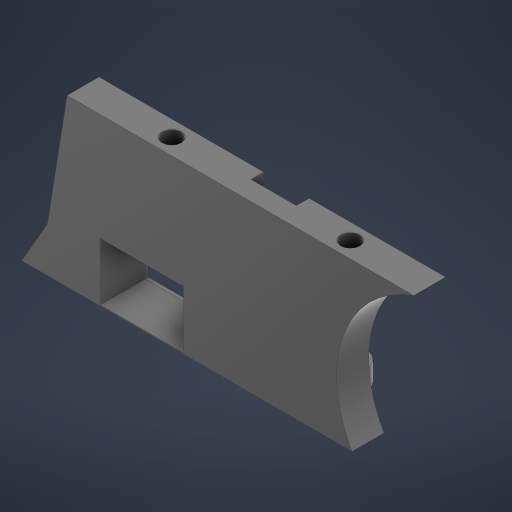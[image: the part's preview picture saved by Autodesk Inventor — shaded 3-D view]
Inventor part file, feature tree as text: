
AUTODESK INVENTOR PART (.ipt)
format: ipt  version: 2024 (Build 280153000, 153)  size: 302,080 bytes
history: native  units: in
note: dims shown in document units (in); Inventor stores cm internally (conversion verified against a paired STEP export)
features: extrude x7, sketch x7, chamfer x2, fillet x1
ambient origin geometry x8: Origin, YZ Plane, XZ Plane, XY Plane, X Axis, Y Axis, Z Axis, Center Point
bodies: Solid1 (feature_tree)
feature tree (17):
  extrude  "Extrusion1"  Depth=0.315in
  extrude  "Extrusion4"  Depth=0.1969in TaperAngle=0.0deg
  chamfer  "Chamfer2"  Distance=0.0984in Angle=45.0deg
  extrude  "Extrusion5"  Depth=0.5in
  extrude  "Extrusion6"  Depth=0.0787in TaperAngle=0.0deg
  chamfer  "Chamfer3"  Distance=0.0512in
  extrude  "Extrusion8"  Depth=0.1181in TaperAngle=0.0deg
  extrude  "Extrusion9"  Depth=0.0787in TaperAngle=0.0deg
  extrude  "Extrusion10"  [1 undecoded]
  fillet  "Fillet3"  [1 undecoded]
  sketch  "Sketch1"  dims[d1=0.1969in d2=0.0in d31=0.315in]
  sketch  "Sketch4"  dims[d32=0.1575in d33=0.1969in d34=0.0in d35=0.0984in d36=0.1772in d37=45.0deg]
  sketch  "Sketch6"  dims[d39=0.5in d41=0.5in]
  sketch  "Sketch7"  dims[d42=0.25in d43=0.0787in d44=0.0in d45=0.0512in d46=0.0in]
  sketch  "Sketch9"  dims[d47=0.315in d48=0.0787in d49=0.1374in d58=0.1181in d59=0.0in]
  sketch  "Sketch10"  dims[d60=0.0787in d61=0.0in d62=0.0787in d63=0.0in]
  sketch  "Sketch11"  dims[d64=0.1181in]
note: 2 required parameter values undecoded (feature->parameter linkage not recoverable at this tier; creation-order binding heuristic only, values carry confidence <= 0.55)
